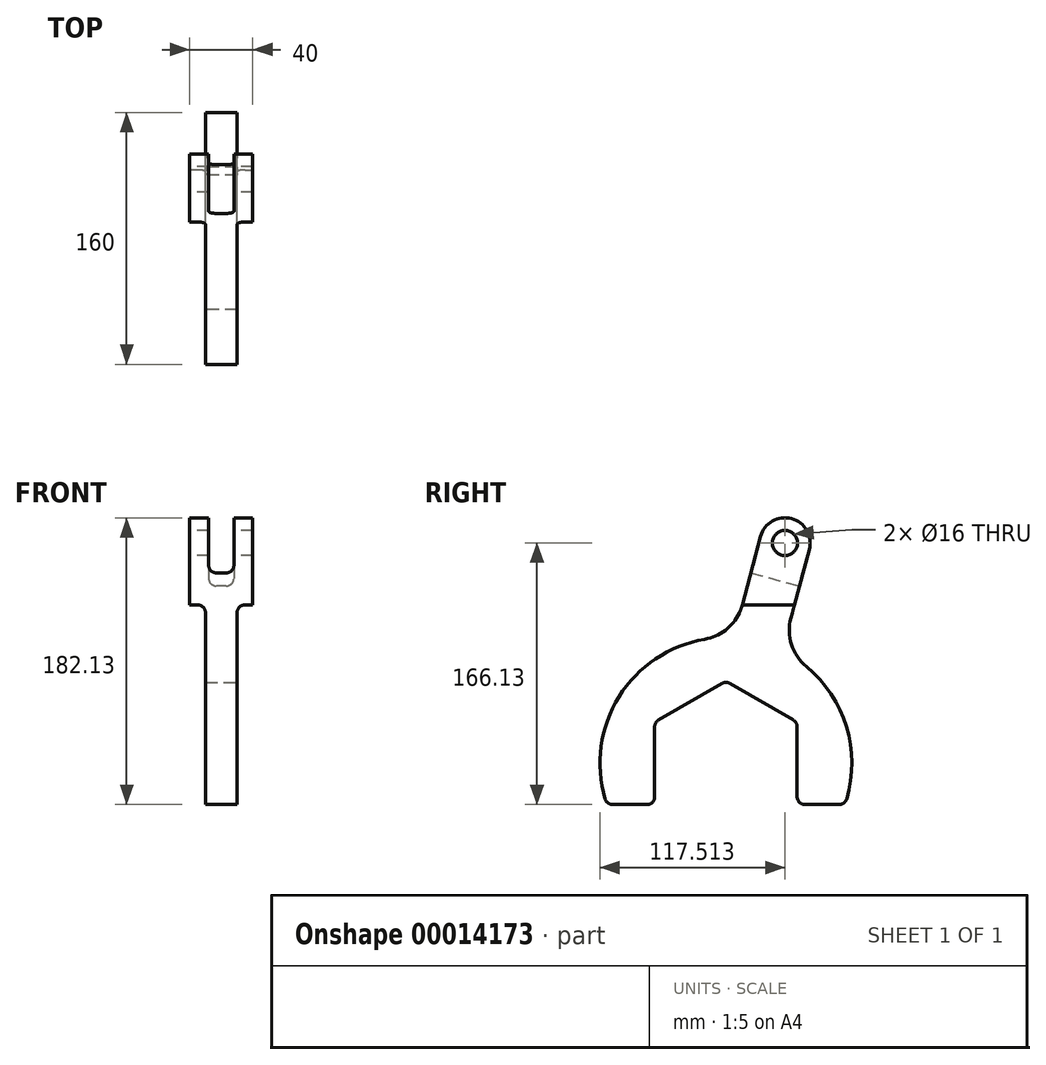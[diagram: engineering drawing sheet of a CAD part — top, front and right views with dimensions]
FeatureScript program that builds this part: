
annotation { "Feature Type Name" : "Feature", "Feature Type Description" : "" }
export const myFeature = defineFeature(function(context is Context, id is Id, definition is map)
    precondition{}
    {
        {
            var Q0;
            Q0=qCreatedBy(makeId("Right.planeOp"),FACE);
            var sketch = newSketch(context, id + "F0", { "sketchPlane" : qUnion([Q0])});
            skCircle(sketch, "E0.cCircle", {"center": v(0, 0) * mm, "radius": 45.25 * mm, "construction": true});
            skLineSegment(sketch, "E0.0", {"start": v(-45.25, -26.13) * mm, "end": v(-45.25, 26.13) * mm});
            skLineSegment(sketch, "E0.1", {"start": v(-45.25, 26.13) * mm, "end": v(0, 52.25) * mm});
            skLineSegment(sketch, "E0.2", {"start": v(0, 52.25) * mm, "end": v(45.25, 26.13) * mm});
            skLineSegment(sketch, "E0.3", {"start": v(45.25, 26.13) * mm, "end": v(45.25, -26.13) * mm});
            skLineSegment(sketch, "E0.4", {"start": v(22.63, -39.19) * mm, "end": v(21.51, -39.83) * mm});
            skPoint(sketch, "E0.0.midPoint", {"position": v(-45.25, 0) * mm});
            skLineSegment(sketch, "E1", {"start": v(0, 0) * mm, "end": v(0, 140) * mm, "construction": true});
            skLineSegment(sketch, "E2", {"start": v(0, 140) * mm, "end": v(132.53, 140) * mm, "construction": true});
            skLineSegment(sketch, "E3", {"start": v(0, 0) * mm, "end": v(37.51, 140) * mm, "construction": true});
            skCircle(sketch, "E4", {"center": v(37.51, 140) * mm, "radius": 8 * mm});
            skArc(sketch, "E5", {"start": v(75.61, -26.13) * mm, "mid": v(77.05, 21.53) * mm, "end": v(51.12, 61.53) * mm});
            skLineSegment(sketch, "E6", {"start": v(37.51, 140) * mm, "end": v(37.51, 210.9) * mm, "construction": true});
            skLineSegment(sketch, "E7", {"start": v(-75.61, -26.13) * mm, "end": v(-45.25, -26.13) * mm});
            skPoint(sketch, "E8.orphan", {"position": v(53.51, -53.76) * mm});
            skArc(sketch, "E9.trimOffspring", {"start": v(-13.5, 78.85) * mm, "mid": v(-68.85, 40.74) * mm, "end": v(-75.61, -26.13) * mm});
            skPoint(sketch, "E10.orphan", {"position": v(-113.23, -26.13) * mm});
            skLineSegment(sketch, "E11.trimOffspring", {"start": v(45.25, -26.13) * mm, "end": v(75.61, -26.13) * mm});
            skPoint(sketch, "E12.visualSharp", {"position": v(61.16, 51.57) * mm});
            skPoint(sketch, "E13.newPointA", {"position": v(21.51, -53.76) * mm});
            skLineSegment(sketch, "E14.0", {"start": v(41.32, 92.37) * mm, "end": v(52.97, 135.86) * mm});
            skCircle(sketch, "E15", {"center": v(37.51, 140) * mm, "radius": 16 * mm});
            skLineSegment(sketch, "E16.0.MirrorCS", {"start": v(10.4, 100.66) * mm, "end": v(22.06, 144.14) * mm});
            skPoint(sketch, "E17.orphan", {"position": v(-15.45, 4.14) * mm});
            skPoint(sketch, "E18.orphan", {"position": v(15.45, -4.14) * mm});
            skPoint(sketch, "E19.visualSharp", {"position": v(4.83, 79.85) * mm});
            skArc(sketch, "E19.filletArc", {"start": v(-13.5, 78.85) * mm, "mid": v(1.64, 86.25) * mm, "end": v(10.4, 100.66) * mm});
            skPoint(sketch, "E20.visualSharp", {"position": v(35.74, 71.57) * mm});
            skArc(sketch, "E20.filletArc", {"start": v(41.32, 92.37) * mm, "mid": v(41.7, 75.52) * mm, "end": v(51.12, 61.53) * mm});
            skSolve(sketch);
        }
        {
            var Q0;
            Q0=qSketchRegion(id+"F0",true);
            extrude(context, id + "F1", {"entities" : qUnion([Q0]), "endBound" : BoundingType.SYMMETRIC, "depth" : 40 * mm});
        }
        {
            var Q0;
            Q0=makeQuery(id+"F1.opExtrude","SWEPT_EDGE",EDGE,{"disambiguationData":[OSD([sQuery(id+"F0.wireOp",EDGE,"E0.3"),sQuery(id+"F0.wireOp",EDGE,"E11.trimOffspring")])]});
            var Q1;
            Q1=makeQuery(id+"F1.opExtrude","SWEPT_EDGE",EDGE,{"disambiguationData":[OSD([sQuery(id+"F0.wireOp",EDGE,"E0.0"),sQuery(id+"F0.wireOp",EDGE,"E7")])]});
            var Q2;
            Q2=makeQuery(id+"F1.opExtrude","SWEPT_EDGE",EDGE,{"disambiguationData":[OSD([sQuery(id+"F0.wireOp",EDGE,"E7"),sQuery(id+"F0.wireOp",EDGE,"E9.trimOffspring")])]});
            var Q3;
            Q3=makeQuery(id+"F1.opExtrude","SWEPT_EDGE",EDGE,{"disambiguationData":[OSD([sQuery(id+"F0.wireOp",EDGE,"E5"),sQuery(id+"F0.wireOp",EDGE,"E11.trimOffspring")])]});
            fillet(context, id + "F2", {"entities" : qUnion([Q0, Q1, Q2, Q3]), "radius" : 5 * mm, "tangentPropagation" : true, "allowEdgeOverflow" : false});
        }
        {
            var Q0;
            Q0=makeQuery(id+"F1.opExtrude","SWEPT_EDGE",EDGE,{"disambiguationData":[OSD([sQuery(id+"F0.wireOp",EDGE,"E0.2"),sQuery(id+"F0.wireOp",EDGE,"E0.3")])]});
            var Q1;
            Q1=makeQuery(id+"F1.opExtrude","SWEPT_EDGE",EDGE,{"disambiguationData":[OSD([sQuery(id+"F0.wireOp",EDGE,"E0.1"),sQuery(id+"F0.wireOp",EDGE,"E0.2")])]});
            var Q2;
            Q2=makeQuery(id+"F1.opExtrude","SWEPT_EDGE",EDGE,{"disambiguationData":[OSD([sQuery(id+"F0.wireOp",EDGE,"E0.0"),sQuery(id+"F0.wireOp",EDGE,"E0.1")])]});
            fillet(context, id + "F3", {"entities" : qUnion([Q0, Q1, Q2]), "radius" : 5 * mm, "tangentPropagation" : true, "allowEdgeOverflow" : false});
        }
        {
            var Q0;
            Q0=makeQuery(id+"F1.opExtrude","CAP_FACE",FACE,{"disambiguationData":[OSD([sQuery(id+"F0.wireOp",EDGE,"E0.0"),sQuery(id+"F0.wireOp",EDGE,"E0.1"),sQuery(id+"F0.wireOp",EDGE,"E0.2"),sQuery(id+"F0.wireOp",EDGE,"E0.3"),sQuery(id+"F0.wireOp",EDGE,"E4"),sQuery(id+"F0.wireOp",EDGE,"E5"),sQuery(id+"F0.wireOp",EDGE,"E7"),sQuery(id+"F0.wireOp",EDGE,"E9.trimOffspring"),sQuery(id+"F0.wireOp",EDGE,"E11.trimOffspring"),sQuery(id+"F0.wireOp",EDGE,"E14.0"),sQuery(id+"F0.wireOp",EDGE,"E15"),sQuery(id+"F0.wireOp",EDGE,"E16.0.MirrorCS"),sQuery(id+"F0.wireOp",EDGE,"E19.filletArc"),sQuery(id+"F0.wireOp",EDGE,"E20.filletArc")])],"isStart":false});
            var sketch = newSketch(context, id + "F4", { "sketchPlane" : qUnion([Q0])});
            skLineSegment(sketch, "E21", {"start": v(0, 0) * mm, "end": v(130.77, 0) * mm, "construction": true});
            skLineSegment(sketch, "E22", {"start": v(10.4, 100.66) * mm, "end": v(43.54, 100.66) * mm});
            skArc(sketch, "E23.0", {"start": v(-13.5, 78.85) * mm, "mid": v(1.64, 86.25) * mm, "end": v(10.4, 100.66) * mm});
            skArc(sketch, "E24.0", {"start": v(-13.5, 78.85) * mm, "mid": v(-67.87, 42.35) * mm, "end": v(-76.76, -22.53) * mm});
            skLineSegment(sketch, "E25.0.0", {"start": v(-71.96, -26.13) * mm, "end": v(-50.25, -26.13) * mm});
            skArc(sketch, "E25.0.1", {"start": v(-50.25, -26.13) * mm, "mid": v(-46.71, -24.66) * mm, "end": v(-45.25, -21.13) * mm});
            skLineSegment(sketch, "E25.0.2", {"start": v(-45.25, -21.13) * mm, "end": v(-45.25, 23.24) * mm});
            skArc(sketch, "E25.0.3", {"start": v(-45.25, 23.24) * mm, "mid": v(-44.58, 25.74) * mm, "end": v(-42.75, 27.57) * mm});
            skLineSegment(sketch, "E25.0.4", {"start": v(-42.75, 27.57) * mm, "end": v(-2.5, 50.8) * mm});
            skArc(sketch, "E25.0.5", {"start": v(-2.5, 50.8) * mm, "mid": v(0, 51.48) * mm, "end": v(2.5, 50.8) * mm});
            skLineSegment(sketch, "E25.0.6", {"start": v(2.5, 50.8) * mm, "end": v(42.75, 27.57) * mm});
            skArc(sketch, "E25.0.7", {"start": v(42.75, 27.57) * mm, "mid": v(44.58, 25.74) * mm, "end": v(45.25, 23.24) * mm});
            skLineSegment(sketch, "E25.0.8", {"start": v(45.25, 23.24) * mm, "end": v(45.25, -21.13) * mm});
            skArc(sketch, "E25.0.9", {"start": v(45.25, -21.13) * mm, "mid": v(46.71, -24.66) * mm, "end": v(50.25, -26.13) * mm});
            skLineSegment(sketch, "E25.0.10", {"start": v(50.25, -26.13) * mm, "end": v(71.96, -26.13) * mm});
            skArc(sketch, "E25.0.11", {"start": v(71.96, -26.13) * mm, "mid": v(74.96, -25.13) * mm, "end": v(76.76, -22.53) * mm});
            skArc(sketch, "E25.0.12", {"start": v(76.76, -22.53) * mm, "mid": v(76.52, 23.34) * mm, "end": v(51.12, 61.53) * mm});
            skArc(sketch, "E25.0.13", {"start": v(51.12, 61.53) * mm, "mid": v(41.7, 75.52) * mm, "end": v(41.32, 92.37) * mm});
            skLineSegment(sketch, "E25.0.14", {"start": v(41.32, 92.37) * mm, "end": v(43.54, 100.66) * mm});
            skArc(sketch, "E25.0.17", {"start": v(10.4, 100.66) * mm, "mid": v(1.64, 86.25) * mm, "end": v(-13.5, 78.85) * mm});
            skArc(sketch, "E25.0.19", {"start": v(-76.76, -22.53) * mm, "mid": v(-74.96, -25.13) * mm, "end": v(-71.96, -26.13) * mm});
            skPoint(sketch, "E25.0.15.end.orphan", {"position": v(22.06, 144.14) * mm});
            skPoint(sketch, "E26.orphan", {"position": v(52.97, 135.86) * mm});
            skSolve(sketch);
        }
        {
            var Q0;
            Q0 = qSketchRegion(id + "F4", true);
            extrude(context, id + "F5", {"entities" : qUnion([Q0]), "operationType" : NewBodyOperationType.REMOVE, "oppositeDirection" : true, "depth" : 10 * mm});
        }
        {
            var Q0;
            Q0=makeQuery(id+"F1.opExtrude","CAP_FACE",FACE,{"disambiguationData":[OSD([sQuery(id+"F0.wireOp",EDGE,"E0.0"),sQuery(id+"F0.wireOp",EDGE,"E0.1"),sQuery(id+"F0.wireOp",EDGE,"E0.2"),sQuery(id+"F0.wireOp",EDGE,"E0.3"),sQuery(id+"F0.wireOp",EDGE,"E4"),sQuery(id+"F0.wireOp",EDGE,"E5"),sQuery(id+"F0.wireOp",EDGE,"E7"),sQuery(id+"F0.wireOp",EDGE,"E9.trimOffspring"),sQuery(id+"F0.wireOp",EDGE,"E11.trimOffspring"),sQuery(id+"F0.wireOp",EDGE,"E14.0"),sQuery(id+"F0.wireOp",EDGE,"E15"),sQuery(id+"F0.wireOp",EDGE,"E16.0.MirrorCS"),sQuery(id+"F0.wireOp",EDGE,"E19.filletArc"),sQuery(id+"F0.wireOp",EDGE,"E20.filletArc")])],"isStart":true});
            var sketch = newSketch(context, id + "F6", { "sketchPlane" : qUnion([Q0])});
            skLineSegment(sketch, "E27.0.0", {"start": v(45.25, 23.24) * mm, "end": v(45.25, -21.13) * mm});
            skArc(sketch, "E27.0.1", {"start": v(45.25, -21.13) * mm, "mid": v(46.71, -24.66) * mm, "end": v(50.25, -26.13) * mm});
            skLineSegment(sketch, "E27.0.2", {"start": v(50.25, -26.13) * mm, "end": v(71.96, -26.13) * mm});
            skArc(sketch, "E27.0.3", {"start": v(71.96, -26.13) * mm, "mid": v(74.96, -25.13) * mm, "end": v(76.76, -22.53) * mm});
            skArc(sketch, "E27.0.4", {"start": v(76.76, -22.53) * mm, "mid": v(67.87, 42.35) * mm, "end": v(13.5, 78.85) * mm});
            skArc(sketch, "E27.0.5", {"start": v(13.5, 78.85) * mm, "mid": v(-1.64, 86.25) * mm, "end": v(-10.4, 100.66) * mm});
            skArc(sketch, "E27.0.7", {"start": v(-22.06, 144.14) * mm, "mid": v(-41.65, 155.45) * mm, "end": v(-52.97, 135.86) * mm});
            skLineSegment(sketch, "E27.0.8", {"start": v(-43.54, 100.66) * mm, "end": v(-41.32, 92.37) * mm});
            skArc(sketch, "E27.0.9", {"start": v(-41.32, 92.37) * mm, "mid": v(-41.7, 75.52) * mm, "end": v(-51.12, 61.53) * mm});
            skArc(sketch, "E27.0.10", {"start": v(-51.12, 61.53) * mm, "mid": v(-76.52, 23.34) * mm, "end": v(-76.76, -22.53) * mm});
            skArc(sketch, "E27.0.11", {"start": v(-76.76, -22.53) * mm, "mid": v(-74.96, -25.13) * mm, "end": v(-71.96, -26.13) * mm});
            skLineSegment(sketch, "E27.0.12", {"start": v(-71.96, -26.13) * mm, "end": v(-50.25, -26.13) * mm});
            skArc(sketch, "E27.0.13", {"start": v(-50.25, -26.13) * mm, "mid": v(-46.71, -24.66) * mm, "end": v(-45.25, -21.13) * mm});
            skLineSegment(sketch, "E27.0.14", {"start": v(-45.25, -21.13) * mm, "end": v(-45.25, 23.24) * mm});
            skArc(sketch, "E27.0.15", {"start": v(-45.25, 23.24) * mm, "mid": v(-44.58, 25.74) * mm, "end": v(-42.75, 27.57) * mm});
            skLineSegment(sketch, "E27.0.16", {"start": v(-42.75, 27.57) * mm, "end": v(-2.5, 50.8) * mm});
            skArc(sketch, "E27.0.17", {"start": v(-2.5, 50.8) * mm, "mid": v(0, 51.48) * mm, "end": v(2.5, 50.8) * mm});
            skLineSegment(sketch, "E27.0.18", {"start": v(2.5, 50.8) * mm, "end": v(42.75, 27.57) * mm});
            skArc(sketch, "E27.0.19", {"start": v(42.75, 27.57) * mm, "mid": v(44.58, 25.74) * mm, "end": v(45.25, 23.24) * mm});
            skLineSegment(sketch, "E28.0", {"start": v(-10.4, 100.66) * mm, "end": v(-43.54, 100.66) * mm});
            skSolve(sketch);
        }
        {
            var Q0;
            Q0 = qSketchRegion(id + "F6", true);
            extrude(context, id + "F7", {"entities" : qUnion([Q0]), "operationType" : NewBodyOperationType.REMOVE, "oppositeDirection" : true, "depth" : 10 * mm});
        }
        {
            var Q0;
            Q0=makeQuery(id+"F7.boolean.opBoolean","COPY",EDGE,{"derivedFrom":makeQuery(id+"F7.opExtrude","CAP_EDGE",EDGE,{"disambiguationData":[OSD([sQuery(id+"F6.wireOp",EDGE,"E28.0")])],"isStart":false})});
            var Q1;
            Q1=makeQuery(id+"F7.boolean.opBoolean","COPY",EDGE,{"derivedFrom":makeQuery(id+"F7.opExtrude","CAP_EDGE",EDGE,{"disambiguationData":[OSD([sQuery(id+"F6.wireOp",EDGE,"E28.0")])],"isStart":true})});
            var Q2;
            Q2=makeQuery(id+"F5.boolean.opBoolean","COPY",EDGE,{"derivedFrom":makeQuery(id+"F5.opExtrude","CAP_EDGE",EDGE,{"disambiguationData":[OSD([sQuery(id+"F4.wireOp",EDGE,"E22")])],"isStart":false})});
            var Q3;
            Q3=makeQuery(id+"F5.boolean.opBoolean","COPY",EDGE,{"derivedFrom":makeQuery(id+"F5.opExtrude","CAP_EDGE",EDGE,{"disambiguationData":[OSD([sQuery(id+"F4.wireOp",EDGE,"E22")])],"isStart":true})});
            fillet(context, id + "F8", {"entities" : qUnion([Q0, Q1, Q2, Q3]), "radius" : 5 * mm, "tangentPropagation" : true, "allowEdgeOverflow" : false});
        }
        {
            var Q0;
            Q0=makeQuery(id+"F1.opExtrude","SWEPT_FACE",FACE,{"disambiguationData":[OSD([sQuery(id+"F0.wireOp",EDGE,"E14.0")])]});
            var sketch = newSketch(context, id + "F9", { "sketchPlane" : qUnion([Q0])});
            skLineSegment(sketch, "E29.0", {"start": v(-20, 144.94) * mm, "end": v(20, 144.94) * mm, "construction": true});
            skLineSegment(sketch, "E30", {"start": v(-20, 160.94) * mm, "end": v(20, 160.94) * mm, "construction": true});
            skLineSegment(sketch, "E31.0.MirrorCS", {"start": v(-20, 128.94) * mm, "end": v(20, 128.94) * mm, "construction": true});
            skLineSegment(sketch, "E32.0", {"start": v(-20, 120.94) * mm, "end": v(20, 120.94) * mm, "construction": true});
            skLineSegment(sketch, "E33", {"start": v(0, 160.94) * mm, "end": v(0, 105.69) * mm, "construction": true});
            skLineSegment(sketch, "E34.0", {"start": v(8, 160.94) * mm, "end": v(8, 105.69) * mm, "construction": true});
            skLineSegment(sketch, "E35.0.MirrorCS", {"start": v(-8, 160.94) * mm, "end": v(-8, 105.69) * mm, "construction": true});
            skLineSegment(sketch, "E36.bottom", {"start": v(-8, 160.94) * mm, "end": v(8, 160.94) * mm});
            skLineSegment(sketch, "E36.top", {"start": v(-8, 120.94) * mm, "end": v(8, 120.94) * mm});
            skLineSegment(sketch, "E36.left", {"start": v(-8, 160.94) * mm, "end": v(-8, 120.94) * mm});
            skLineSegment(sketch, "E36.right", {"start": v(8, 160.94) * mm, "end": v(8, 120.94) * mm});
            skSolve(sketch);
        }
        {
            var Q0;
            Q0 = qSketchRegion(id + "F9", true);
            extrude(context, id + "F10", {"entities" : qUnion([Q0]), "operationType" : NewBodyOperationType.REMOVE, "endBound" : BoundingType.THROUGH_ALL, "oppositeDirection" : true, "depth" : 25 * mm});
        }
        {
            var Q0;
            Q0=makeQuery(id+"F10.boolean.opBoolean","COPY",EDGE,{"derivedFrom":makeQuery(id+"F10.opExtrude","SWEPT_EDGE",EDGE,{"disambiguationData":[OSD([sQuery(id+"F9.wireOp",EDGE,"E36.top"),sQuery(id+"F9.wireOp",EDGE,"E36.left")])]})});
            var Q1;
            Q1=makeQuery(id+"F10.boolean.opBoolean","COPY",EDGE,{"derivedFrom":makeQuery(id+"F10.opExtrude","SWEPT_EDGE",EDGE,{"disambiguationData":[OSD([sQuery(id+"F9.wireOp",EDGE,"E36.top"),sQuery(id+"F9.wireOp",EDGE,"E36.right")])]})});
            fillet(context, id + "F11", {"entities" : qUnion([Q0, Q1]), "radius" : 5 * mm, "tangentPropagation" : true, "allowEdgeOverflow" : false});
        }
    });
